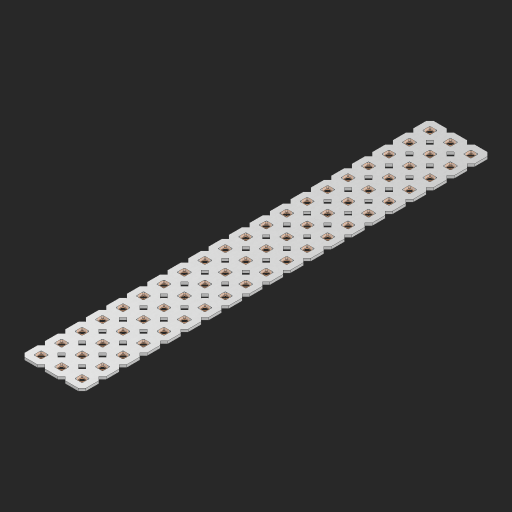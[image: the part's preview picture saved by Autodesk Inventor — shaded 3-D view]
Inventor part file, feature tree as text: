
AUTODESK INVENTOR PART (.ipt)
format: ipt  version: 2023 (Build 270158000, 158)  size: 970,752 bytes
history: native  units: in
note: dims shown in document units (in); Inventor stores cm internally (conversion verified against a paired STEP export)
features: other x61, extrude x59, sketch x2, pattern_linear x1
ambient origin geometry x8: Origin, YZ Plane, XZ Plane, XY Plane, X Axis, Y Axis, Z Axis, Center Point
bodies: Solid1 (feature_tree), Body (feature_tree)
feature tree (123):
  pattern_linear  "Rectangular Pattern1"  Spacing1=0.09in  [1 undecoded]
  sketch  "Sketch1"  dims[d1=0.5in]
  sketch  "Sketch2"  dims[d2=0.182in d3=0.09in d4=0.09in d5=0.09in d6=0.09in d7=0.09in d8=0.09in d9=0.09in d10=0.09in d11=0.02in d13=0.0in d14=0.172in d15=0.0625in d16=0.0in d19=0.5in d22=0.5in]
  other  "Srf1"
  other  "Srf126"
  other  "Srf127"
  other  "Srf128"
  other  "Srf129"
  other  "Srf130"
  other  "Srf131"
  other  "Srf250"
  other  "Srf251"
  other  "Srf252"
  other  "Srf253"
  other  "Srf254"
  other  "Srf255"
  other  "Srf256"
  other  "Srf257"
  other  "Srf258"
  other  "Srf259"
  other  "Srf260"
  other  "Srf261"
  other  "Srf262"
  other  "Srf268"
  other  "Srf269"
  other  "Srf270"
  other  "Srf271"
  other  "Srf272"
  other  "Srf273"
  other  "Srf274"
  other  "Srf275"
  other  "Srf276"
  other  "Srf277"
  other  "Srf278"
  other  "Srf279"
  other  "Srf280"
  other  "Srf281"
  other  "Srf282"
  other  "Srf283"
  other  "Srf284"
  other  "Srf285"
  other  "Srf286"
  other  "Srf287"
  other  "Srf293"
  other  "Srf294"
  other  "Srf295"
  other  "Srf296"
  other  "Srf297"
  other  "Srf298"
  other  "Srf299"
  other  "Srf300"
  other  "Srf301"
  other  "Srf302"
  other  "Srf303"
  other  "Srf304"
  other  "Srf305"
  other  "Srf306"
  other  "Srf307"
  other  "Srf308"
  other  "Srf309"
  other  "Srf310"
  other  "Srf311"
  other  "Srf312"
  other  "Circle"
  extrude  "ExtrusionSrf126"  Depth=0.09in
  extrude  "ExtrusionSrf127"  Depth=0.09in
  extrude  "ExtrusionSrf128"  Depth=0.09in
  extrude  "ExtrusionSrf129"  Depth=0.09in
  extrude  "ExtrusionSrf130"  Depth=0.09in
  extrude  "ExtrusionSrf131"  Depth=0.09in
  extrude  "ExtrusionSrf250"  Depth=0.09in
  extrude  "ExtrusionSrf251"  Depth=0.02in
  extrude  "ExtrusionSrf252"  TaperAngle=0.0deg  [1 undecoded]
  extrude  "ExtrusionSrf253"  Depth=0.5in
  extrude  "ExtrusionSrf254"  Depth=0.0625in TaperAngle=0.0deg
  extrude  "ExtrusionSrf255"  Depth=0.5in
  extrude  "ExtrusionSrf256"  Depth=0.5in
  extrude  "ExtrusionSrf257"  [1 undecoded]
  extrude  "ExtrusionSrf258"  [1 undecoded]
  extrude  "ExtrusionSrf259"  [1 undecoded]
  extrude  "ExtrusionSrf260"  [1 undecoded]
  extrude  "ExtrusionSrf261"  [1 undecoded]
  extrude  "ExtrusionSrf262"  [1 undecoded]
  extrude  "ExtrusionSrf268"  [1 undecoded]
  extrude  "ExtrusionSrf269"  [1 undecoded]
  extrude  "ExtrusionSrf270"  [1 undecoded]
  extrude  "ExtrusionSrf271"  [1 undecoded]
  extrude  "ExtrusionSrf272"  [1 undecoded]
  extrude  "ExtrusionSrf273"  [1 undecoded]
  extrude  "ExtrusionSrf274"  [1 undecoded]
  extrude  "ExtrusionSrf275"  [1 undecoded]
  extrude  "ExtrusionSrf276"  [1 undecoded]
  extrude  "ExtrusionSrf277"  [1 undecoded]
  extrude  "ExtrusionSrf278"  [1 undecoded]
  extrude  "ExtrusionSrf279"  [1 undecoded]
  extrude  "ExtrusionSrf280"  [1 undecoded]
  extrude  "ExtrusionSrf281"  [1 undecoded]
  extrude  "ExtrusionSrf282"  [1 undecoded]
  extrude  "ExtrusionSrf283"  [1 undecoded]
  extrude  "ExtrusionSrf284"  [1 undecoded]
  extrude  "ExtrusionSrf285"  [1 undecoded]
  extrude  "ExtrusionSrf286"  [1 undecoded]
  extrude  "ExtrusionSrf287"  [1 undecoded]
  extrude  "ExtrusionSrf293"  [1 undecoded]
  extrude  "ExtrusionSrf294"  [1 undecoded]
  extrude  "ExtrusionSrf295"  [1 undecoded]
  extrude  "ExtrusionSrf296"  [1 undecoded]
  extrude  "ExtrusionSrf297"  [1 undecoded]
  extrude  "ExtrusionSrf298"  [1 undecoded]
  extrude  "ExtrusionSrf299"  [1 undecoded]
  extrude  "ExtrusionSrf300"  [1 undecoded]
  extrude  "ExtrusionSrf301"  [1 undecoded]
  extrude  "ExtrusionSrf302"  [1 undecoded]
  extrude  "ExtrusionSrf303"  [1 undecoded]
  extrude  "ExtrusionSrf304"  [1 undecoded]
  extrude  "ExtrusionSrf305"  [1 undecoded]
  extrude  "ExtrusionSrf306"  [1 undecoded]
  extrude  "ExtrusionSrf307"  [1 undecoded]
  extrude  "ExtrusionSrf308"  [1 undecoded]
  extrude  "ExtrusionSrf309"  [1 undecoded]
  extrude  "ExtrusionSrf310"  [1 undecoded]
  extrude  "ExtrusionSrf311"  [1 undecoded]
  extrude  "ExtrusionSrf312"  [1 undecoded]
note: 48 required parameter values undecoded (feature->parameter linkage not recoverable at this tier; creation-order binding heuristic only, values carry confidence <= 0.55)
